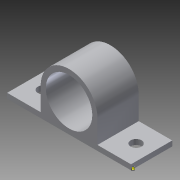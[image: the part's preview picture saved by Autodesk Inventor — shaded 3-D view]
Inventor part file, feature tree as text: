
AUTODESK INVENTOR PART (.ipt)
format: ipt  version: 2013 (Build 170138000, 138)  size: 141,312 bytes
history: native  units: in
note: dims shown in document units (in); Inventor stores cm internally (conversion verified against a paired STEP export)
features: extrude x3, sketch x2
ambient origin geometry x8: Origin, YZ Plane, XZ Plane, XY Plane, X Axis, Y Axis, Z Axis, Center Point
bodies: Solid1 (feature_tree)
feature tree (5):
  extrude  "Extrusion1"  Depth=1.5in
  extrude  "Extrusion2"  Depth=0.6875in
  extrude  "Extrusion3"  Depth=1.125in
  sketch  "Sketch2"  dims[d0=1.5in d1=1.5in]
  sketch  "Sketch3"  dims[d2=0.125in d3=0.6875in d4=1.125in d6=1.0in d7=0.0in d8=0.266in d11=1.0in d12=0.0in d13=0.375in d14=0.266in d15=0.375in d16=0.125in d17=1.0in d18=0.0in]
